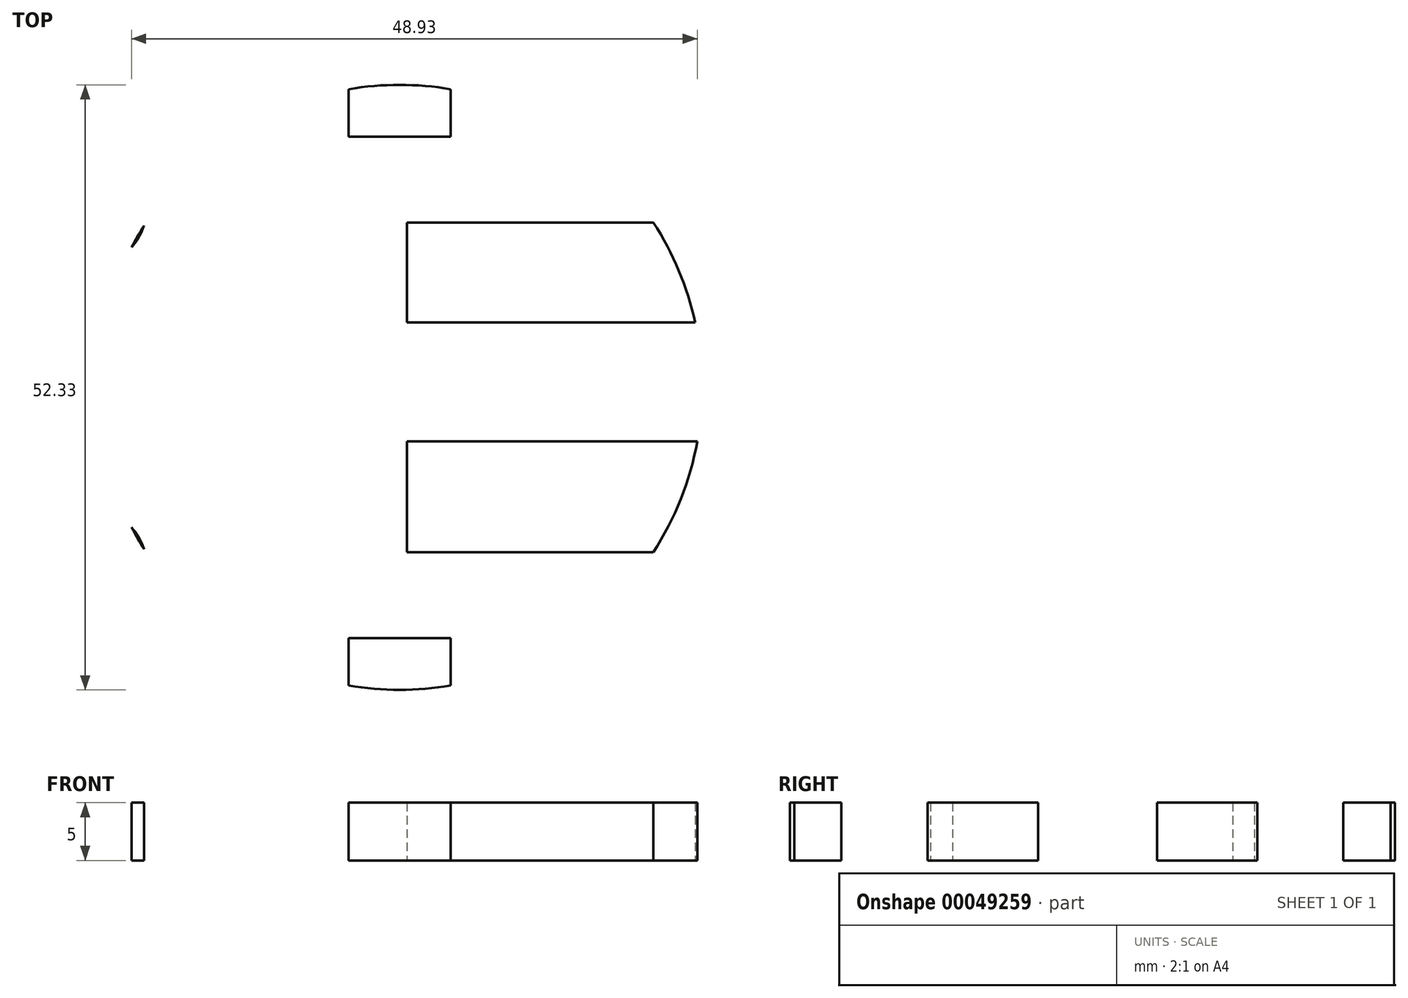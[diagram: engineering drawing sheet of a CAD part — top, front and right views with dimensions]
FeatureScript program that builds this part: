
annotation { "Feature Type Name" : "Feature", "Feature Type Description" : "" }
export const myFeature = defineFeature(function(context is Context, id is Id, definition is map)
    precondition{}
    {
        {
            var Q0;
            Q0=qCreatedBy(makeId("Top.planeOp"),FACE);
            var sketch = newSketch(context, id + "F0", { "sketchPlane" : qUnion([Q0])});
            skArc(sketch, "E0", {"start": v(14.83, 5.85) * mm, "mid": v(-36.89, -0.23) * mm, "end": v(15.01, -4.45) * mm});
            skPoint(sketch, "E1", {"position": v(-35.93, -0.58) * mm});
            skLineSegment(sketch, "E2", {"start": v(14.83, 5.85) * mm, "end": v(-27.17, 5.85) * mm});
            skLineSegment(sketch, "E3", {"start": v(15.01, -4.45) * mm, "end": v(-26.98, -4.45) * mm});
            skLineSegment(sketch, "E4", {"start": v(-27.17, 5.85) * mm, "end": v(-27.17, -4.45) * mm});
            skLineSegment(sketch, "E5", {"start": v(-37.6, 10.74) * mm, "end": v(-63.56, 10.74) * mm});
            skLineSegment(sketch, "E6", {"start": v(-37.6, -10.25) * mm, "end": v(-63.56, -10.25) * mm});
            skArc(sketch, "E7", {"start": v(-63.56, 10.74) * mm, "mid": v(-74.06, 0.24) * mm, "end": v(-63.56, -10.25) * mm});
            skLineSegment(sketch, "E8", {"start": v(11.2, 14.5) * mm, "end": v(-10.1, 14.5) * mm});
            skLineSegment(sketch, "E9", {"start": v(-10.1, 14.5) * mm, "end": v(-10.1, 5.85) * mm});
            skLineSegment(sketch, "E10", {"start": v(11.2, -14.02) * mm, "end": v(-10.1, -14.02) * mm});
            skLineSegment(sketch, "E11", {"start": v(-10.1, -14.02) * mm, "end": v(-10.1, -4.45) * mm});
            skLineSegment(sketch, "E12", {"start": v(-6.33, 26.03) * mm, "end": v(-6.33, 21.93) * mm});
            skLineSegment(sketch, "E13", {"start": v(-6.33, 21.93) * mm, "end": v(-15.13, 21.93) * mm});
            skLineSegment(sketch, "E14", {"start": v(-15.13, 21.93) * mm, "end": v(-15.13, 26.03) * mm});
            skLineSegment(sketch, "E15", {"start": v(-6.33, -25.55) * mm, "end": v(-6.33, -21.46) * mm});
            skLineSegment(sketch, "E16", {"start": v(-6.33, -21.46) * mm, "end": v(-15.13, -21.46) * mm});
            skLineSegment(sketch, "E17", {"start": v(-15.13, -21.46) * mm, "end": v(-15.13, -25.55) * mm});
            skArc(sketch, "E18", {"start": v(-37.6, 10.74) * mm, "mid": v(-34.65, 11.7) * mm, "end": v(-32.83, 14.23) * mm});
            skArc(sketch, "E19", {"start": v(-32.83, -13.77) * mm, "mid": v(-34.64, -11.23) * mm, "end": v(-37.6, -10.25) * mm});
            skCircle(sketch, "E20", {"center": v(-63.56, 0.24) * mm, "radius": 6 * mm});
            skCircle(sketch, "E21", {"center": v(-63.56, 0.24) * mm, "radius": 9 * mm});
            skSolve(sketch);
        }
        {
            var Q0;
            {var subQ3=sQuery(id+"F0.wireOp",EDGE,"E8");Q0=makeQuery(id+"F0.imprint","IMPRINT",FACE,{"disambiguationData":[TD([[makeQuery(id+"F0.imprint","IMPRINT",EDGE,{"derivedFrom":subQ3}),1.0]])]});}
            var Q1;
            {var subQ0=sQuery(id+"F0.wireOp",EDGE,"E12");Q1=makeQuery(id+"F0.imprint","IMPRINT",FACE,{"disambiguationData":[TD([[makeQuery(id+"F0.imprint","IMPRINT",EDGE,{"derivedFrom":subQ0}),-1.0]])]});}
            var Q2;
            {var subQ0=sQuery(id+"F0.wireOp",EDGE,"E18");var subQ1=sQuery(id+"F0.wireOp",EDGE,"E0");var subQ2=makeQuery(id+"F0.imprint","INTERSECT",VERTEX,{"disambiguationData":[OD(0.0)],"derivedFrom":[subQ1,subQ0]});Q2=makeQuery(id+"F0.imprint","IMPRINT",FACE,{"disambiguationData":[TD([[makeQuery(id+"F0.imprint","IMPRINT",EDGE,{"disambiguationData":[TD([[subQ2,-1.0]])],"derivedFrom":subQ1}),1.0]])]});}
            var Q3;
            {var subQ0=sQuery(id+"F0.wireOp",EDGE,"E19");var subQ1=sQuery(id+"F0.wireOp",EDGE,"E0");var subQ2=makeQuery(id+"F0.imprint","INTERSECT",VERTEX,{"disambiguationData":[OD(0.0)],"derivedFrom":[subQ1,subQ0]});Q3=makeQuery(id+"F0.imprint","IMPRINT",FACE,{"disambiguationData":[TD([[makeQuery(id+"F0.imprint","IMPRINT",EDGE,{"disambiguationData":[TD([[subQ2,1.0]])],"derivedFrom":subQ1}),1.0]])]});}
            var Q4;
            {var subQ0=sQuery(id+"F0.wireOp",EDGE,"E15");Q4=makeQuery(id+"F0.imprint","IMPRINT",FACE,{"disambiguationData":[TD([[makeQuery(id+"F0.imprint","IMPRINT",EDGE,{"derivedFrom":subQ0}),1.0]])]});}
            var Q5;
            {var subQ3=sQuery(id+"F0.wireOp",EDGE,"E10");Q5=makeQuery(id+"F0.imprint","IMPRINT",FACE,{"disambiguationData":[TD([[makeQuery(id+"F0.imprint","IMPRINT",EDGE,{"derivedFrom":subQ3}),-1.0]])]});}
            var Q6;
            Q6=makeQuery(id+"F0.imprint","IMPRINT",FACE,{"disambiguationData":[TD([[makeQuery(id+"F0.imprint","IMPRINT",EDGE,{"derivedFrom":sQuery(id+"F0.wireOp",EDGE,"6c50f5a8-e45b-4b68-96a0-fe3e2d22da39")}),-1.0]])]});
            extrude(context, id + "F1", {"entities" : qUnion([Q0, Q1, Q2, Q3, Q4, Q5, Q6]), "depth" : 5 * mm});
        }
    });
